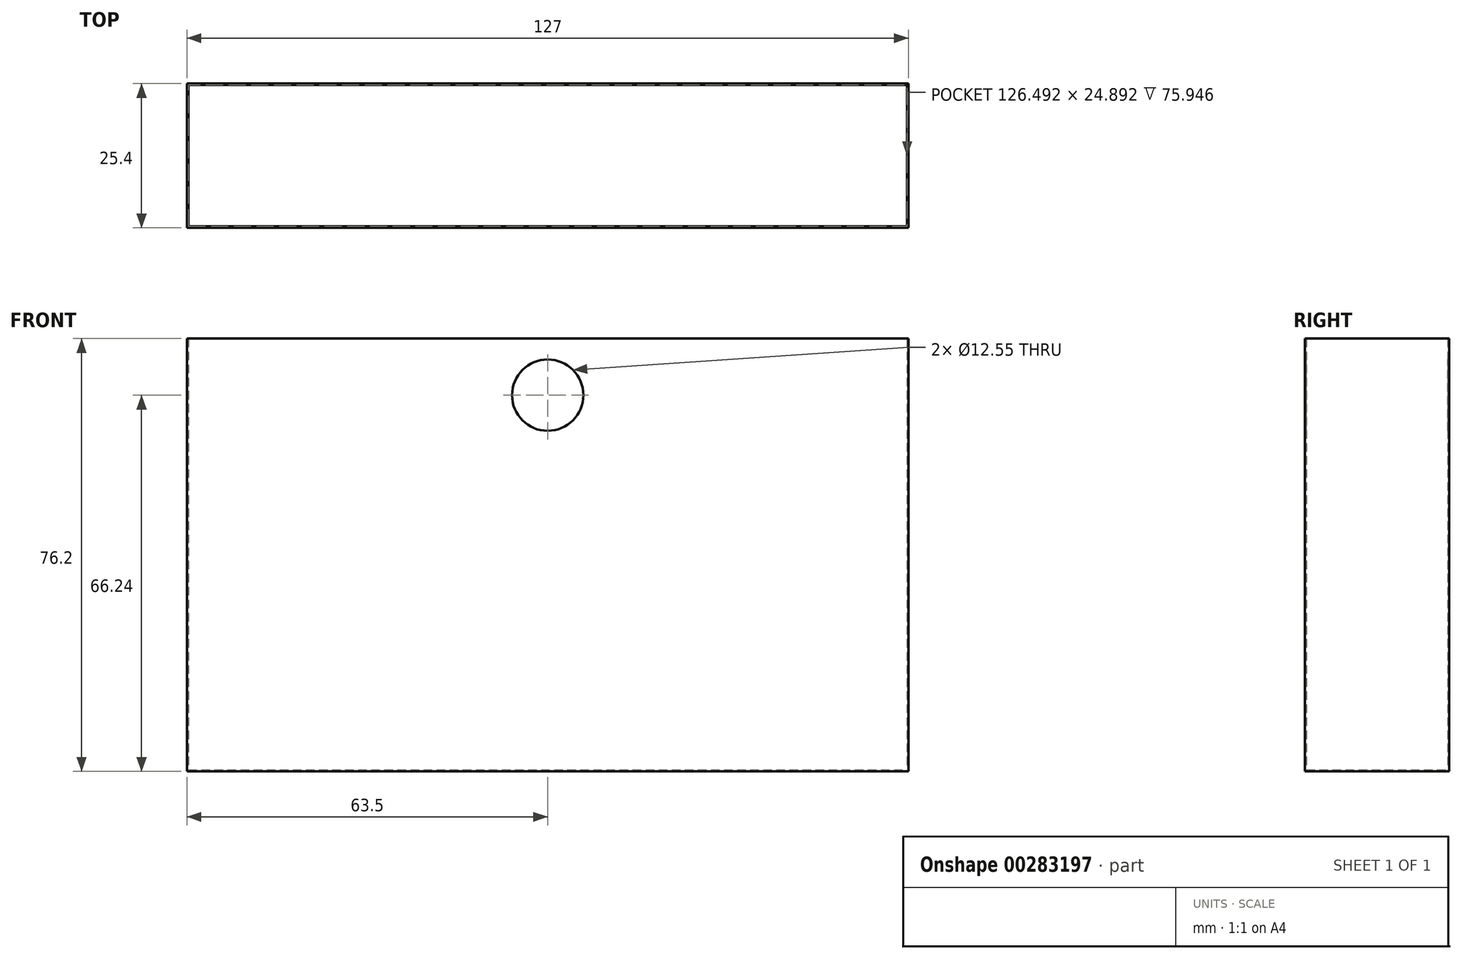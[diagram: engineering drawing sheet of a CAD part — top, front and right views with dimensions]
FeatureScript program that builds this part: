
annotation { "Feature Type Name" : "Feature", "Feature Type Description" : "" }
export const myFeature = defineFeature(function(context is Context, id is Id, definition is map)
    precondition{}
    {
        {
            var Q0;
            Q0=qCreatedBy(makeId("Front.planeOp"),FACE);
            var sketch = newSketch(context, id + "F0", { "sketchPlane" : qUnion([Q0])});
            skLineSegment(sketch, "E0.bottom", {"start": v(-63.5, 38.1) * mm, "end": v(63.5, 38.1) * mm});
            skLineSegment(sketch, "E0.top", {"start": v(-63.5, -38.1) * mm, "end": v(63.5, -38.1) * mm});
            skLineSegment(sketch, "E0.left", {"start": v(-63.5, 38.1) * mm, "end": v(-63.5, -38.1) * mm});
            skLineSegment(sketch, "E0.right", {"start": v(63.5, 38.1) * mm, "end": v(63.5, -38.1) * mm});
            skPoint(sketch, "E0.middle", {"position": v(0, 0) * mm});
            skSolve(sketch);
        }
        {
            var Q0;
            Q0=makeQuery(id+"F0.imprint","IMPRINT",FACE,{"disambiguationData":[TD([[makeQuery(id+"F0.imprint","IMPRINT",EDGE,{"derivedFrom":sQuery(id+"F0.wireOp",EDGE,"E0.bottom")}),-1.0]])]});
            extrude(context, id + "F1", {"entities" : qUnion([Q0]), "depth" : 25.4 * mm});
        }
        {
            var Q0;
            Q0=makeQuery(id+"F1.opExtrude","SWEPT_FACE",FACE,{"disambiguationData":[OSD([sQuery(id+"F0.wireOp",EDGE,"E0.bottom")])]});
            shell(context, id + "F2", {"entities" : qUnion([Q0]), "thickness" : 0.25 * mm});
        }
        {
            var Q0;
            Q0=makeQuery(id+"F1.opExtrude","CAP_FACE",FACE,{"disambiguationData":[OSD([sQuery(id+"F0.wireOp",EDGE,"E0.bottom"),sQuery(id+"F0.wireOp",EDGE,"E0.top"),sQuery(id+"F0.wireOp",EDGE,"E0.left"),sQuery(id+"F0.wireOp",EDGE,"E0.right")])],"isStart":false});
            var sketch = newSketch(context, id + "F3", { "sketchPlane" : qUnion([Q0])});
            skCircle(sketch, "E1", {"center": v(0, 28.14) * mm, "radius": 6.27 * mm});
            skSolve(sketch);
        }
        {
            var Q0;
            Q0=makeQuery(id+"F3.imprint","IMPRINT",FACE,{"disambiguationData":[TD([[makeQuery(id+"F3.imprint","IMPRINT",EDGE,{"derivedFrom":sQuery(id+"F3.wireOp",EDGE,"E1")}),1.0]])]});
            extrude(context, id + "F4", {"entities" : qUnion([Q0]), "operationType" : NewBodyOperationType.REMOVE, "oppositeDirection" : true, "depth" : 50.8 * mm});
        }
    });
